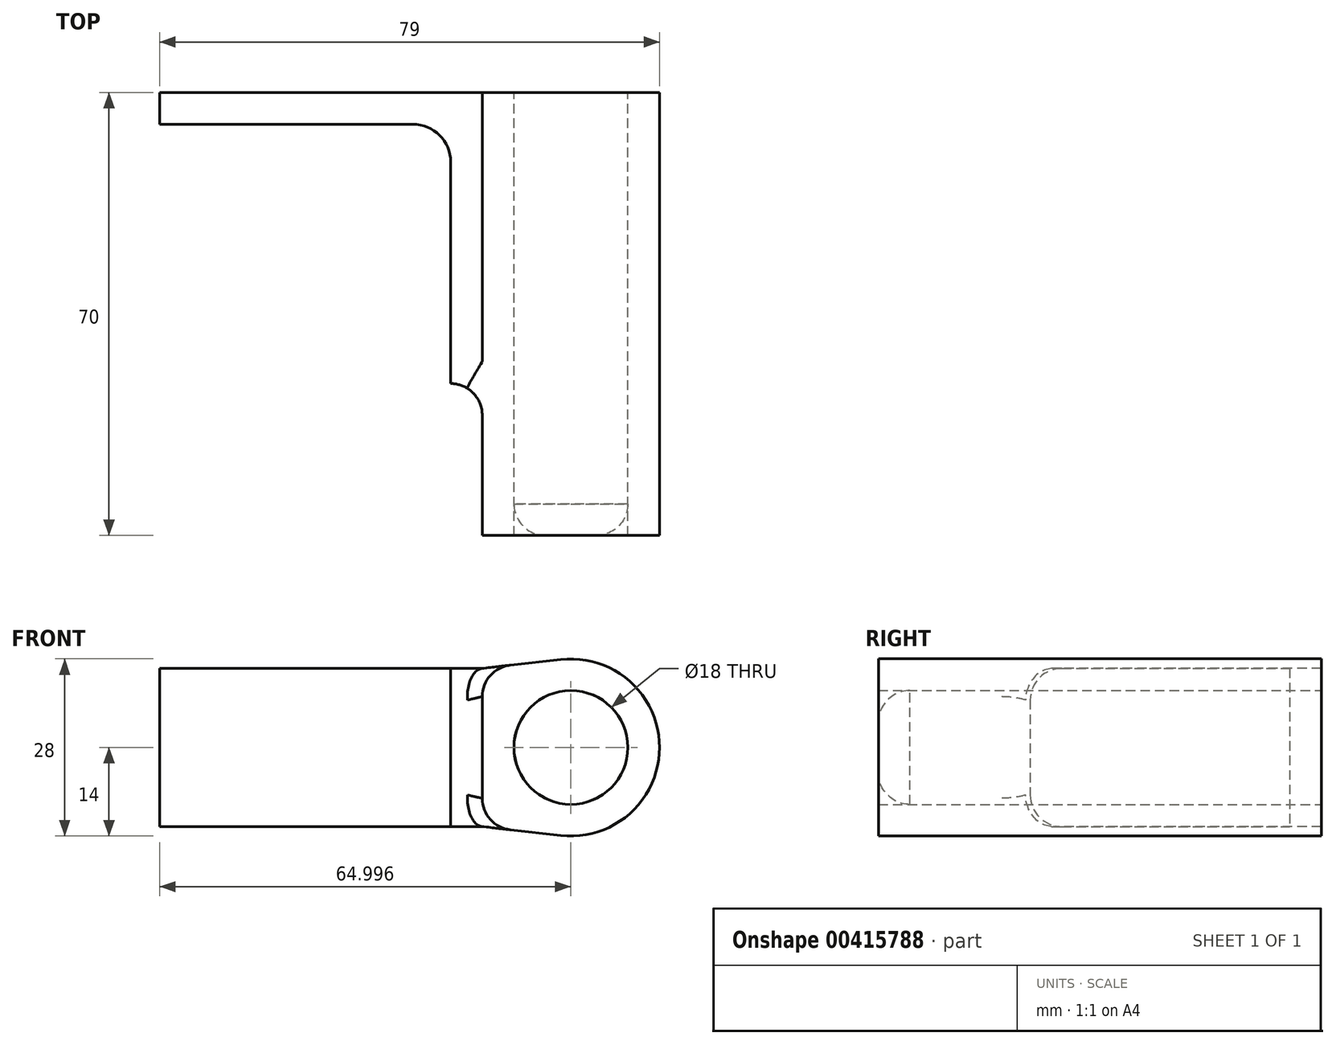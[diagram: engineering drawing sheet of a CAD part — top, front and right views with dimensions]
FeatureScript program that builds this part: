
annotation { "Feature Type Name" : "Feature", "Feature Type Description" : "" }
export const myFeature = defineFeature(function(context is Context, id is Id, definition is map)
    precondition{}
    {
        {
            var Q0;
            Q0=qCreatedBy(makeId("Top.planeOp"),FACE);
            var sketch = newSketch(context, id + "F0", { "sketchPlane" : qUnion([Q0])});
            skLineSegment(sketch, "E0", {"start": v(-34.71, 5.25) * mm, "end": v(16.29, 5.25) * mm});
            skLineSegment(sketch, "E1", {"start": v(16.29, 5.25) * mm, "end": v(16.29, -40.75) * mm});
            skLineSegment(sketch, "E2", {"start": v(16.29, -40.75) * mm, "end": v(11.29, -40.75) * mm});
            skLineSegment(sketch, "E3", {"start": v(11.29, -40.75) * mm, "end": v(11.29, -5.75) * mm});
            skLineSegment(sketch, "E4", {"start": v(5.29, 0.25) * mm, "end": v(-34.71, 0.25) * mm});
            skLineSegment(sketch, "E5", {"start": v(-34.71, 5.25) * mm, "end": v(-34.71, 0.25) * mm});
            skPoint(sketch, "E6.visualSharp", {"position": v(11.29, 0.25) * mm});
            skArc(sketch, "E6.filletArc", {"start": v(11.29, -5.75) * mm, "mid": v(9.53, -1.5) * mm, "end": v(5.29, 0.25) * mm});
            skSolve(sketch);
        }
        {
            var Q0;
            Q0 = qSketchRegion(id + "F0", true);
            extrude(context, id + "F1", {"entities" : qUnion([Q0]), "depth" : 25 * mm});
        }
        {
            var Q0;
            Q0=makeQuery(id+"F1.opExtrude","SWEPT_FACE",FACE,{"disambiguationData":[OSD([sQuery(id+"F0.wireOp",EDGE,"E0")])]});
            var sketch = newSketch(context, id + "F2", { "sketchPlane" : qUnion([Q0])});
            skCircle(sketch, "E7", {"center": v(-30.29, 12.5) * mm, "radius": 9 * mm});
            skArc(sketch, "E8", {"start": v(-28.7, 26.41) * mm, "mid": v(-44.29, 12.5) * mm, "end": v(-28.7, -1.41) * mm});
            skLineSegment(sketch, "E9", {"start": v(-16.29, 25) * mm, "end": v(-28.7, 26.41) * mm});
            skLineSegment(sketch, "E10", {"start": v(-16.29, 0) * mm, "end": v(-28.7, -1.41) * mm});
            skLineSegment(sketch, "E11", {"start": v(-16.29, 25) * mm, "end": v(-16.29, 0) * mm});
            skSolve(sketch);
        }
        {
            var Q0;
            Q0=makeQuery(id+"F2.imprint","IMPRINT",FACE,{"disambiguationData":[TD([[makeQuery(id+"F2.imprint","IMPRINT",EDGE,{"derivedFrom":sQuery(id+"F2.wireOp",EDGE,"E7")}),-1.0]])]});
            extrude(context, id + "F3", {"entities" : qUnion([Q0]), "operationType" : NewBodyOperationType.ADD, "oppositeDirection" : true, "depth" : 70 * mm});
        }
        {
            var Q0;
            Q0=makeQuery(id+"F3.opExtrude","CAP_FACE",FACE,{"disambiguationData":[OSD([sQuery(id+"F2.wireOp",EDGE,"E7"),sQuery(id+"F2.wireOp",EDGE,"E8"),sQuery(id+"F2.wireOp",EDGE,"E9"),sQuery(id+"F2.wireOp",EDGE,"E10"),sQuery(id+"F2.wireOp",EDGE,"E11")])],"isStart":false});
            var sketch = newSketch(context, id + "F4", { "sketchPlane" : qUnion([Q0])});
            skCircle(sketch, "E12", {"center": v(30.29, 12.5) * mm, "radius": 9 * mm});
            skSolve(sketch);
        }
        {
            var Q0;
            Q0 = qSketchRegion(id + "F4", true);
            extrude(context, id + "F5", {"entities" : qUnion([Q0]), "operationType" : NewBodyOperationType.ADD, "oppositeDirection" : true, "depth" : 5 * mm});
        }
        {
            var Q0;
            Q0=makeQuery(id+"F1.opExtrude","SWEPT_EDGE",EDGE,{"disambiguationData":[OSD([sQuery(id+"F0.wireOp",EDGE,"E1"),sQuery(id+"F0.wireOp",EDGE,"E2")])]});
            var Q1;
            Q1=makeQuery(id+"F1.opExtrude","CAP_EDGE",EDGE,{"disambiguationData":[OSD([sQuery(id+"F0.wireOp",EDGE,"E0")])],"isStart":true});
            var Q2;
            Q2=makeQuery(id+"F1.opExtrude","SWEPT_EDGE",EDGE,{"disambiguationData":[OSD([sQuery(id+"F0.wireOp",EDGE,"E0"),sQuery(id+"F0.wireOp",EDGE,"E5")])]});
            var Q3;
            Q3=makeQuery(id+"F1.opExtrude","CAP_EDGE",EDGE,{"disambiguationData":[OSD([sQuery(id+"F0.wireOp",EDGE,"E0")])],"isStart":false});
            var Q4;
            Q4=makeQuery(id+"F3.opExtrude","CAP_EDGE",EDGE,{"disambiguationData":[OSD([sQuery(id+"F2.wireOp",EDGE,"E9")])],"isStart":true});
            var Q5;
            Q5=makeQuery(id+"F5.boolean.opBoolean","MERGE",FACE,{"derivedFrom":[makeQuery(id+"F3.opExtrude","CAP_FACE",FACE,{"disambiguationData":[OSD([sQuery(id+"F2.wireOp",EDGE,"E7"),sQuery(id+"F2.wireOp",EDGE,"E8"),sQuery(id+"F2.wireOp",EDGE,"E9"),sQuery(id+"F2.wireOp",EDGE,"E10"),sQuery(id+"F2.wireOp",EDGE,"E11")])],"isStart":false}),makeQuery(id+"F5.opExtrude","CAP_FACE",FACE,{"disambiguationData":[OSD([sQuery(id+"F4.wireOp",EDGE,"E12")])],"isStart":true})]});
            fillet(context, id + "F6", {"entities" : qUnion([Q0, Q1, Q2, Q3, Q4, Q5]), "radius" : 5 * mm, "tangentPropagation" : true, "allowEdgeOverflow" : false});
        }
        {
            var Q0;
            Q0=makeQuery(id+"F3.boolean.opBoolean","SPLIT",EDGE,{"derivedFrom":makeQuery(id+"F3.opExtrude","SWEPT_EDGE",EDGE,{"disambiguationData":[OSD([sQuery(id+"F0.wireOp",EDGE,"E0"),sQuery(id+"F2.wireOp",EDGE,"E10"),sQuery(id+"F2.wireOp",EDGE,"E11")])]})});
            var Q1;
            Q1=makeQuery(id+"F3.boolean.opBoolean","SPLIT",EDGE,{"derivedFrom":makeQuery(id+"F3.opExtrude","SWEPT_EDGE",EDGE,{"disambiguationData":[OSD([sQuery(id+"F0.wireOp",EDGE,"E0"),sQuery(id+"F2.wireOp",EDGE,"E9"),sQuery(id+"F2.wireOp",EDGE,"E11")])]})});
            fillet(context, id + "F7", {"entities" : qUnion([Q0, Q1]), "radius" : 5 * mm, "tangentPropagation" : true, "allowEdgeOverflow" : false});
        }
    });
